# Revit family: Rückflussverhinderer 2623
name_source: partatom
category: Rohrzubehör
units: mm (PartAtom-declared; Revit-internal decimal feet)

## family parameters
Arbeitsebenenbasiert = Nein
Beim Laden mit Abzugskörper schneiden = Nein
Bemaßung runder Anschluss = Durchmesser verwenden
Gemeinsam genutzt = Nein
Immer vertikal = Ja
OmniClass-Nummer = 23.65.55.14
OmniClass-Titel = Valves for Liquid Services
Teiletyp = Unterbricht

## types (1)
- Rückflussverhinderer 2623
    Anwendung = Kann in Zentralheizungsanlagen, Energiesystemen, Konstruktionen und Maschinenbauanlagen überall verwendet werden, um Rückschläge zu verhindern.
Dieses Produkt kann mit verschiedenen Medien betrieben werden, im allgemeinen wird es jedoch mit klaren Flüssigkeiten benutzt.
Das Ventil kann in jeder Position benutzt werden.
Die Strömungsrichtung ist mit einem Pfeil am Gehäuse angegeben.
Das Rückschlagventil wird federbelastet mittels einer Axialführung und kann sowohl bei niedrigen als auch bei hohen Drücken arbeiten.
Zum Messen sind zwei Bohrungen im Gehäuse ausgeführt in welchen jeweils ein 1/4 Stopfen montiert ist.
    Außengewinde = gemäß ISO 228
    Dichtung = EPDM
    Endstück = Pressmessing
    Gehäuse = Pressmessing gemäß EN 12420
    H02 = 2 mm  [stored 0.00656168 ft]
    Hersteller = HERZ Armaturen Ges.m.b.H.
    Hinweis = Gemäß Art 33 der REACH-Verordnung (EG Nr. 1907/2006) sind wir verpflichtet, darauf hinzuweisen, dass der Stoff Blei auf der SVHC-Liste geführt wird und dass alle aus Messing bestehenden Bauteile, die in unseren Erzeugnissen verarbeitet sind, mehr als 0,1 % (w/w) Blei (CAS: 7439-92-1 / EINECS: 231-100-4) enthalten.
Da Blei als Legierungsbestandteil fest gebunden ist, sind keine Expositionen zu erwarten und daher sind keine zusätzlichen Angaben zur sicheren Verwendung notwendig.
    Innengewinde = gemäß ISO 228
    Max. Betriebsdruck = 1600000.0 Pa
    Max. Betriebstemperatur = 95 °C
    Medium = klare Flüssigkeiten
    Min. Betriebstemperatur = -10 °C
    Min. Betriebstemperatur (Wasser) = 1 °C
    R01 = 9 mm  [stored 0.0295276 ft]
    Rückschlagventil = POM (Gehäuse), NBR (O-Ring), Edelstahl AISI 302 (Feder)
    S03 = 10 mm  [stored 0.0328084 ft]
    SCTWCODE = 04;14;02
    SCTWSEQ = FW;SBT_TYP_FW="108";2
    SC_NennweiteBerechnet = 0
    Stopfen = Messing
    URL = www.herz-armaturen.at
    Vorgabe-Ansicht = 0 mm  [stored 0 ft]
    W01 = 45.00°

note: [stored X ft] marks values corroborated as IEEE doubles in the binary element streams (Revit-internal decimal feet)
